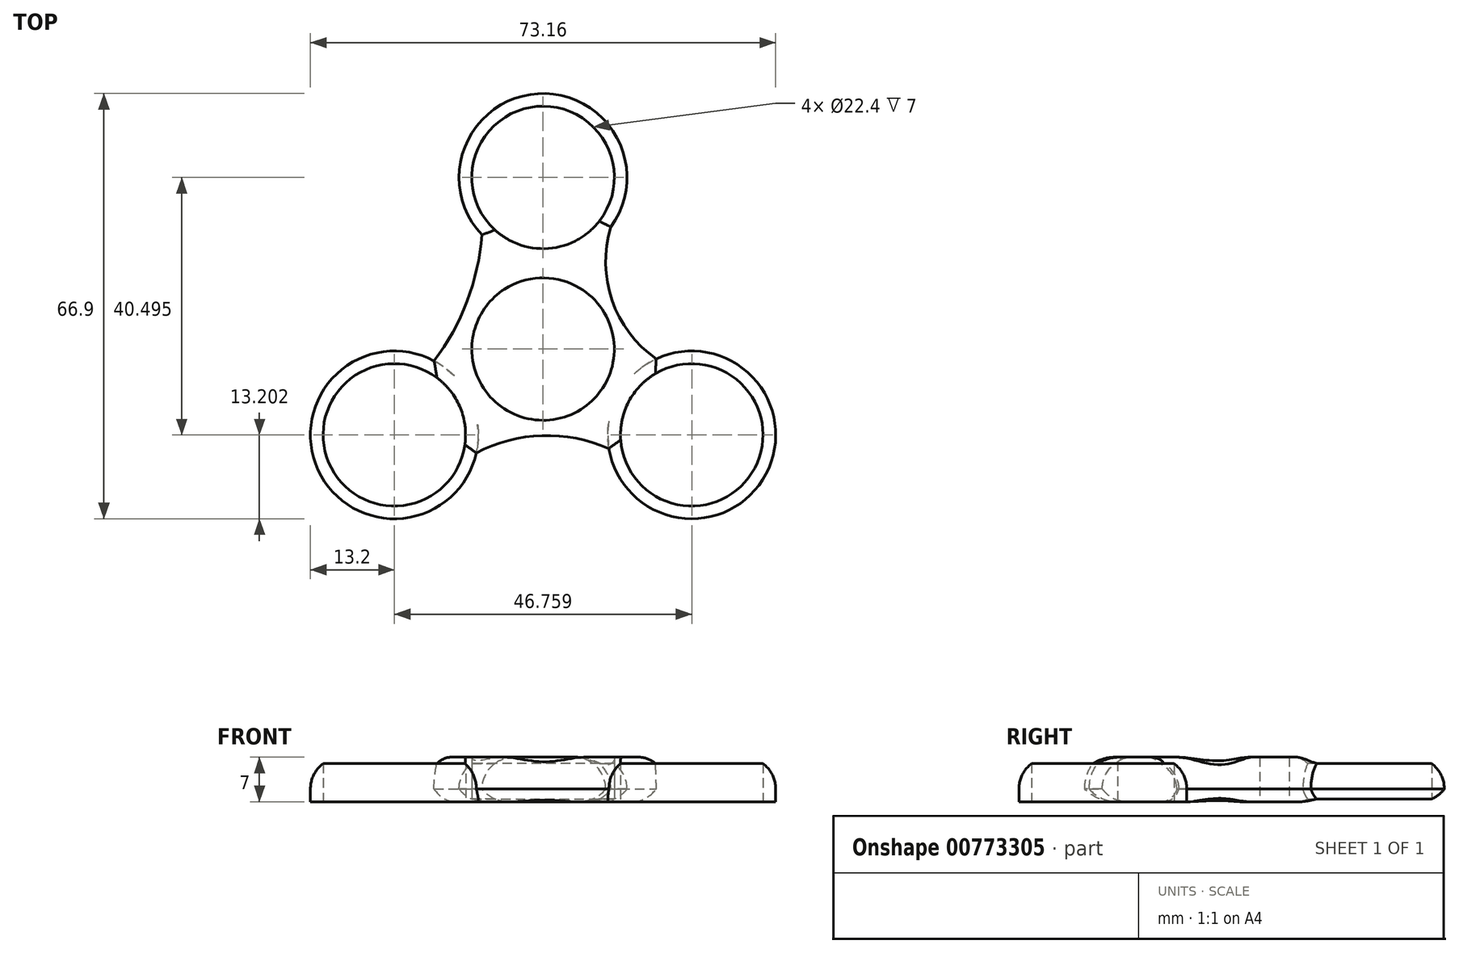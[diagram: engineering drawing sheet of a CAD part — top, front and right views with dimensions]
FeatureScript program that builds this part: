
annotation { "Feature Type Name" : "Feature", "Feature Type Description" : "" }
export const myFeature = defineFeature(function(context is Context, id is Id, definition is map)
    precondition{}
    {
        {
            var Q0;
            Q0=qCreatedBy(makeId("Top.planeOp"),FACE);
            var sketch = newSketch(context, id + "F0", { "sketchPlane" : qUnion([Q0])});
            skCircle(sketch, "E0", {"center": v(0, 0) * mm, "radius": 13.2 * mm});
            skCircle(sketch, "E1", {"center": v(0, 0) * mm, "radius": 11.2 * mm});
            skCircle(sketch, "E2", {"center": v(0, 27) * mm, "radius": 11.2 * mm});
            skCircle(sketch, "E3", {"center": v(0, 27) * mm, "radius": 13.2 * mm});
            skCircle(sketch, "E4.1.0", {"center": v(-23.38, -13.5) * mm, "radius": 11.2 * mm});
            skCircle(sketch, "E4.1.1", {"center": v(-23.38, -13.5) * mm, "radius": 13.2 * mm});
            skCircle(sketch, "E4.2.0", {"center": v(23.38, -13.5) * mm, "radius": 11.2 * mm});
            skCircle(sketch, "E4.2.1", {"center": v(23.38, -13.5) * mm, "radius": 13.2 * mm});
            skArc(sketch, "E5", {"start": v(10.66, 19.21) * mm, "mid": v(10.85, 7.68) * mm, "end": v(17.8, -1.54) * mm});
            skArc(sketch, "E6", {"start": v(-17.15, -1.86) * mm, "mid": v(-11.95, 7.5) * mm, "end": v(-9.63, 17.96) * mm});
            skArc(sketch, "E7", {"start": v(10.36, -15.64) * mm, "mid": v(-0.15, -13.61) * mm, "end": v(-10.5, -16.35) * mm});
            skSolve(sketch);
        }
        {
            var Q0;
            Q0=makeQuery(id+"F0.imprint","IMPRINT",FACE,{"disambiguationData":[TD([[makeQuery(id+"F0.imprint","IMPRINT",EDGE,{"derivedFrom":sQuery(id+"F0.wireOp",EDGE,"E1")}),-1.0]])]});
            var Q1;
            {var subQ4=sQuery(id+"F0.wireOp",EDGE,"E6");Q1=makeQuery(id+"F0.imprint","IMPRINT",FACE,{"disambiguationData":[TD([[makeQuery(id+"F0.imprint","IMPRINT",EDGE,{"derivedFrom":subQ4}),-1.0]])]});}
            var Q2;
            Q2=makeQuery(id+"F0.imprint","IMPRINT",FACE,{"disambiguationData":[TD([[makeQuery(id+"F0.imprint","IMPRINT",EDGE,{"derivedFrom":sQuery(id+"F0.wireOp",EDGE,"E4.1.0")}),-1.0]])]});
            var Q3;
            Q3=makeQuery(id+"F0.imprint","IMPRINT",FACE,{"disambiguationData":[TD([[makeQuery(id+"F0.imprint","IMPRINT",EDGE,{"derivedFrom":sQuery(id+"F0.wireOp",EDGE,"E4.2.0")}),-1.0]])]});
            var Q4;
            Q4=makeQuery(id+"F0.imprint","IMPRINT",FACE,{"disambiguationData":[TD([[makeQuery(id+"F0.imprint","IMPRINT",EDGE,{"derivedFrom":sQuery(id+"F0.wireOp",EDGE,"E2")}),-1.0]])]});
            extrude(context, id + "F1", {"entities" : qUnion([Q0, Q1, Q2, Q3, Q4]), "depth" : 7 * mm, "offsetDistance" : 25 * mm});
        }
        {
            var Q0;
            Q0=makeQuery(id+"F1.opExtrude","CAP_EDGE",EDGE,{"disambiguationData":[OSD([sQuery(id+"F0.wireOp",EDGE,"E3")])],"isStart":false});
            var Q1;
            Q1=makeQuery(id+"F1.opExtrude","CAP_EDGE",EDGE,{"disambiguationData":[OSD([sQuery(id+"F0.wireOp",EDGE,"E5")])],"isStart":false});
            var Q2;
            Q2=makeQuery(id+"F1.opExtrude","CAP_EDGE",EDGE,{"disambiguationData":[OSD([sQuery(id+"F0.wireOp",EDGE,"E4.2.1")])],"isStart":false});
            var Q3;
            Q3=makeQuery(id+"F1.opExtrude","CAP_EDGE",EDGE,{"disambiguationData":[OSD([sQuery(id+"F0.wireOp",EDGE,"E7")])],"isStart":false});
            var Q4;
            Q4=makeQuery(id+"F1.opExtrude","CAP_EDGE",EDGE,{"disambiguationData":[OSD([sQuery(id+"F0.wireOp",EDGE,"E4.1.1")])],"isStart":false});
            var Q5;
            Q5=makeQuery(id+"F1.opExtrude","CAP_EDGE",EDGE,{"disambiguationData":[OSD([sQuery(id+"F0.wireOp",EDGE,"E6")])],"isStart":false});
            fillet(context, id + "F2", {"entities" : qUnion([Q0, Q1, Q2, Q3, Q4, Q5]), "radius" : 5 * mm, "tangentPropagation" : true, "allowEdgeOverflow" : false});
        }
        {
            var Q0;
            Q0=makeQuery(id+"F1.opExtrude","CAP_EDGE",EDGE,{"disambiguationData":[OSD([sQuery(id+"F0.wireOp",EDGE,"E3")])],"isStart":true});
            var Q1;
            Q1=makeQuery(id+"F1.opExtrude","CAP_EDGE",EDGE,{"disambiguationData":[OSD([sQuery(id+"F0.wireOp",EDGE,"E6")])],"isStart":true});
            var Q2;
            Q2=makeQuery(id+"F1.opExtrude","CAP_EDGE",EDGE,{"disambiguationData":[OSD([sQuery(id+"F0.wireOp",EDGE,"E5")])],"isStart":true});
            var Q3;
            Q3=makeQuery(id+"F1.opExtrude","CAP_EDGE",EDGE,{"disambiguationData":[OSD([sQuery(id+"F0.wireOp",EDGE,"E7")])],"isStart":true});
            fillet(context, id + "F3", {"entities" : qUnion([Q0, Q1, Q2, Q3]), "radius" : 5 * mm, "tangentPropagation" : true, "allowEdgeOverflow" : false});
        }
    });
